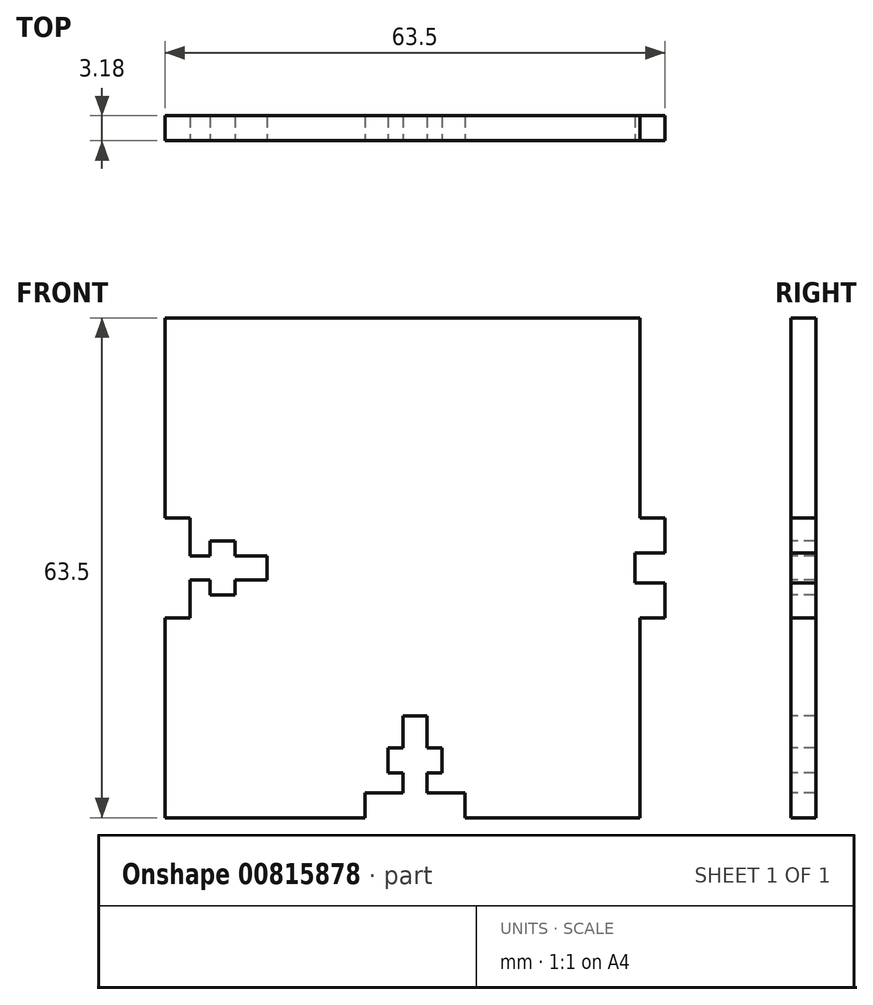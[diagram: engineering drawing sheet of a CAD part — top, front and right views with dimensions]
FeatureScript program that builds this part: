
annotation { "Feature Type Name" : "Feature", "Feature Type Description" : "" }
export const myFeature = defineFeature(function(context is Context, id is Id, definition is map)
    precondition{}
    {
        {
            var Q0;
            Q0=qCreatedBy(makeId("Front.planeOp"),FACE);
            var sketch = newSketch(context, id + "F0", { "sketchPlane" : qUnion([Q0])});
            skLineSegment(sketch, "E0.bottom", {"start": v(31.75, 31.75) * mm, "end": v(-31.75, 31.75) * mm});
            skLineSegment(sketch, "E0.top", {"start": v(31.75, -31.75) * mm, "end": v(-31.75, -31.75) * mm});
            skLineSegment(sketch, "E0.left", {"start": v(31.75, 31.75) * mm, "end": v(31.75, -31.75) * mm});
            skLineSegment(sketch, "E0.right", {"start": v(-31.75, 31.75) * mm, "end": v(-31.75, -31.75) * mm});
            skPoint(sketch, "E0.middle", {"position": v(0, 0) * mm});
            skSolve(sketch);
        }
        {
            var Q0;
            Q0=makeQuery(id+"F0.imprint","IMPRINT",FACE,{"disambiguationData":[TD([[makeQuery(id+"F0.imprint","IMPRINT",EDGE,{"derivedFrom":sQuery(id+"F0.wireOp",EDGE,"E0.bottom")}),1.0]])]});
            extrude(context, id + "F1", {"entities" : qUnion([Q0]), "depth" : 3.17 * mm, "offsetDistance" : 25.4 * mm});
        }
        {
            var Q0;
            Q0=makeQuery(id+"F1.opExtrude","CAP_FACE",FACE,{"disambiguationData":[OSD([sQuery(id+"F0.wireOp",EDGE,"E0.bottom"),sQuery(id+"F0.wireOp",EDGE,"E0.top"),sQuery(id+"F0.wireOp",EDGE,"E0.left"),sQuery(id+"F0.wireOp",EDGE,"E0.right")])],"isStart":false});
            var sketch = newSketch(context, id + "F2", { "sketchPlane" : qUnion([Q0])});
            skLineSegment(sketch, "E1", {"start": v(0, -0.51) * mm, "end": v(0, -31.75) * mm, "construction": true});
            skLineSegment(sketch, "E2.bottom", {"start": v(31.75, 31.75) * mm, "end": v(28.57, 31.75) * mm});
            skLineSegment(sketch, "E2.top", {"start": v(31.75, 6.35) * mm, "end": v(28.58, 6.35) * mm});
            skLineSegment(sketch, "E2.left", {"start": v(31.75, 31.75) * mm, "end": v(31.75, 6.35) * mm});
            skLineSegment(sketch, "E2.right", {"start": v(28.57, 31.75) * mm, "end": v(28.58, 6.35) * mm});
            skLineSegment(sketch, "E3.bottom", {"start": v(31.75, -31.75) * mm, "end": v(28.58, -31.75) * mm});
            skLineSegment(sketch, "E3.top", {"start": v(31.75, -6.35) * mm, "end": v(28.58, -6.35) * mm});
            skLineSegment(sketch, "E3.left", {"start": v(31.75, -31.75) * mm, "end": v(31.75, -6.35) * mm});
            skLineSegment(sketch, "E3.right", {"start": v(28.58, -31.75) * mm, "end": v(28.58, -6.35) * mm});
            skLineSegment(sketch, "E4.bottom", {"start": v(27.94, 1.9) * mm, "end": v(31.75, 1.9) * mm});
            skLineSegment(sketch, "E4.top", {"start": v(27.94, -1.9) * mm, "end": v(31.75, -1.9) * mm});
            skLineSegment(sketch, "E4.left", {"start": v(27.94, 1.9) * mm, "end": v(27.94, -1.9) * mm});
            skPoint(sketch, "E4.middle", {"position": v(31.75, 0) * mm});
            skLineSegment(sketch, "E5", {"start": v(31.75, 0) * mm, "end": v(31.75, 1.9) * mm});
            skLineSegment(sketch, "E6", {"start": v(31.75, 0) * mm, "end": v(31.75, -1.9) * mm});
            skLineSegment(sketch, "E7", {"start": v(0, -31.75) * mm, "end": v(6.35, -31.75) * mm});
            skLineSegment(sketch, "E8", {"start": v(6.35, -31.75) * mm, "end": v(6.35, -28.57) * mm});
            skPoint(sketch, "E9.endSnap0", {"position": v(-3.17, -31.75) * mm});
            skPoint(sketch, "E10.endSnap0", {"position": v(3.18, -31.75) * mm});
            skLineSegment(sketch, "E11", {"start": v(6.35, -28.57) * mm, "end": v(1.52, -28.57) * mm});
            skLineSegment(sketch, "E12", {"start": v(1.52, -28.57) * mm, "end": v(1.52, -26.04) * mm});
            skLineSegment(sketch, "E13", {"start": v(1.52, -26.04) * mm, "end": v(3.43, -26.04) * mm});
            skLineSegment(sketch, "E14", {"start": v(3.43, -26.04) * mm, "end": v(3.43, -22.86) * mm});
            skLineSegment(sketch, "E15", {"start": v(3.43, -22.86) * mm, "end": v(1.52, -22.86) * mm});
            skLineSegment(sketch, "E16", {"start": v(1.52, -22.86) * mm, "end": v(1.52, -18.8) * mm});
            skLineSegment(sketch, "E17", {"start": v(1.52, -18.8) * mm, "end": v(0, -18.8) * mm});
            skLineSegment(sketch, "E18.MirrorCS", {"start": v(-1.52, -28.57) * mm, "end": v(-1.52, -26.04) * mm});
            skLineSegment(sketch, "E19.MirrorCS", {"start": v(-3.43, -22.86) * mm, "end": v(-1.52, -22.86) * mm});
            skLineSegment(sketch, "E20.MirrorCS", {"start": v(-1.52, -22.86) * mm, "end": v(-1.52, -18.8) * mm});
            skLineSegment(sketch, "E21.MirrorCS", {"start": v(0, -31.75) * mm, "end": v(-6.35, -31.75) * mm});
            skLineSegment(sketch, "E22.MirrorCS", {"start": v(-6.35, -28.58) * mm, "end": v(-1.52, -28.58) * mm});
            skLineSegment(sketch, "E23.MirrorCS", {"start": v(-6.35, -31.75) * mm, "end": v(-6.35, -28.58) * mm});
            skLineSegment(sketch, "E24.MirrorCS", {"start": v(-1.52, -26.04) * mm, "end": v(-3.43, -26.04) * mm});
            skLineSegment(sketch, "E25.MirrorCS", {"start": v(-1.52, -18.8) * mm, "end": v(0, -18.8) * mm});
            skLineSegment(sketch, "E26.MirrorCS", {"start": v(-3.43, -26.04) * mm, "end": v(-3.43, -22.86) * mm});
            skLineSegment(sketch, "E27", {"start": v(-31.75, 0) * mm, "end": v(-31.75, -6.35) * mm});
            skLineSegment(sketch, "E28", {"start": v(-31.75, -6.35) * mm, "end": v(-28.57, -6.35) * mm});
            skPoint(sketch, "E29.endSnap0", {"position": v(-31.75, -3.17) * mm});
            skLineSegment(sketch, "E30", {"start": v(-28.57, -6.35) * mm, "end": v(-28.57, -1.52) * mm});
            skLineSegment(sketch, "E31", {"start": v(-28.57, -1.52) * mm, "end": v(-26.03, -1.52) * mm});
            skLineSegment(sketch, "E32", {"start": v(-26.03, -1.52) * mm, "end": v(-26.03, -3.43) * mm});
            skLineSegment(sketch, "E33", {"start": v(-26.03, -3.43) * mm, "end": v(-22.86, -3.43) * mm});
            skLineSegment(sketch, "E34", {"start": v(-22.86, -3.43) * mm, "end": v(-22.86, -1.52) * mm});
            skLineSegment(sketch, "E35", {"start": v(-22.86, -1.52) * mm, "end": v(-18.8, -1.52) * mm});
            skLineSegment(sketch, "E36", {"start": v(-18.8, -1.52) * mm, "end": v(-18.8, 0) * mm});
            skLineSegment(sketch, "E37.MirrorCS", {"start": v(-28.57, 6.35) * mm, "end": v(-28.57, 1.52) * mm});
            skLineSegment(sketch, "E38.MirrorCS", {"start": v(-22.86, 3.43) * mm, "end": v(-22.86, 1.52) * mm});
            skLineSegment(sketch, "E39.MirrorCS", {"start": v(-31.75, 6.35) * mm, "end": v(-28.57, 6.35) * mm});
            skPoint(sketch, "E40.MirrorP", {"position": v(-31.75, 3.17) * mm});
            skLineSegment(sketch, "E41.MirrorCS", {"start": v(-26.03, 1.52) * mm, "end": v(-26.03, 3.43) * mm});
            skLineSegment(sketch, "E42.MirrorCS", {"start": v(-28.57, 1.52) * mm, "end": v(-26.03, 1.52) * mm});
            skLineSegment(sketch, "E43.MirrorCS", {"start": v(-18.8, 1.52) * mm, "end": v(-18.8, 0) * mm});
            skLineSegment(sketch, "E44.MirrorCS", {"start": v(-26.03, 3.43) * mm, "end": v(-22.86, 3.43) * mm});
            skLineSegment(sketch, "E45.MirrorCS", {"start": v(-22.86, 1.52) * mm, "end": v(-18.8, 1.52) * mm});
            skLineSegment(sketch, "E46.MirrorCS", {"start": v(-31.75, 0) * mm, "end": v(-31.75, 6.35) * mm});
            skSolve(sketch);
        }
        {
            var Q0;
            Q0 = qSketchRegion(id + "F2", true);
            extrude(context, id + "F3", {"entities" : qUnion([Q0]), "operationType" : NewBodyOperationType.REMOVE, "oppositeDirection" : true, "depth" : 25.4 * mm, "offsetDistance" : 25.4 * mm});
        }
    });
